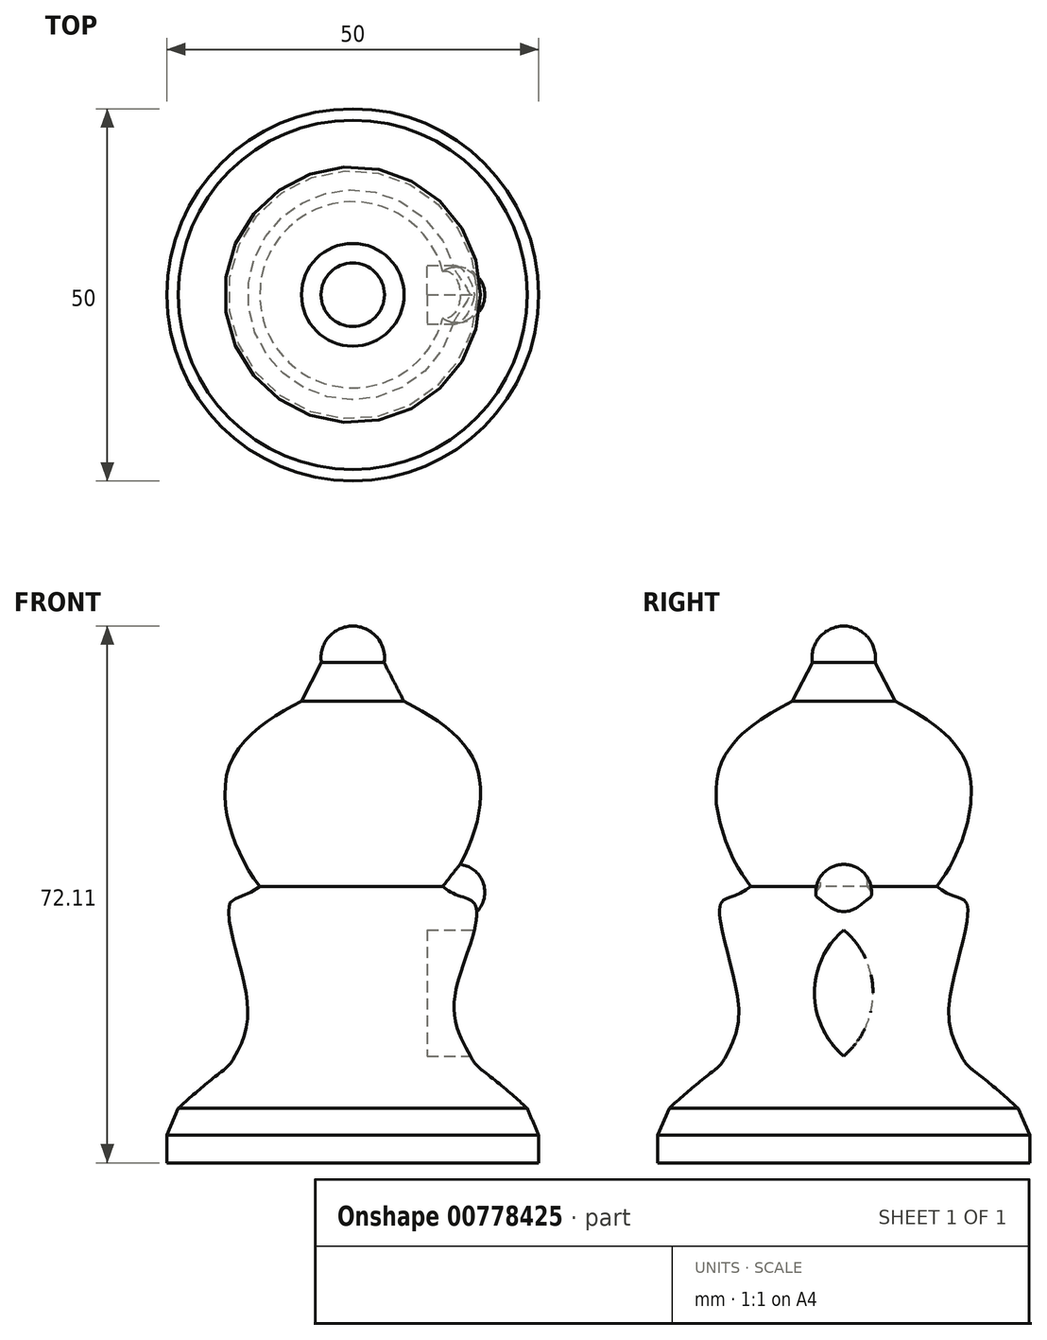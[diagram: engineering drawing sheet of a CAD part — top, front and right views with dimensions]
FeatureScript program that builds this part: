
annotation { "Feature Type Name" : "Feature", "Feature Type Description" : "" }
export const myFeature = defineFeature(function(context is Context, id is Id, definition is map)
    precondition{}
    {
        {
            var Q0;
            Q0=qCreatedBy(makeId("Front.planeOp"),FACE);
            var sketch = newSketch(context, id + "F0", { "sketchPlane" : qUnion([Q0])});
            skLineSegment(sketch, "E0.bottom", {"start": v(0, 0) * mm, "end": v(25, 0) * mm});
            skLineSegment(sketch, "E0.right", {"start": v(25, 0) * mm, "end": v(25, 5.75) * mm});
            skFitSpline(sketch, "E1", {"points": [v(12.5, 37.1) * mm, v(16.59, 34.67) * mm, v(14.3, 22.47) * mm, v(16.59, 13) * mm], "startDerivative": vector(26.77, -20.1) * mm, "endDerivative": vector(18.4, -30.72) * mm});
            skPoint(sketch, "E2.1.internal.snap0", {"position": v(25, 53.36) * mm});
            skFitSpline(sketch, "E2", {"points": [v(12.5, 37.1) * mm, v(16.59, 53.36) * mm, v(0, 65.21) * mm], "startDerivative": vector(22.32, 29.12) * mm, "endDerivative": vector(-44.63, 20.16) * mm});
            skFitSpline(sketch, "E3", {"points": [v(16.59, 13) * mm, v(22.47, 8.23) * mm, v(25, 5.75) * mm], "startDerivative": vector(8.7, -5.97) * mm, "endDerivative": vector(5.16, -5.51) * mm});
            skPoint(sketch, "E4.third.point", {"position": v(0, 67.84) * mm});
            skLineSegment(sketch, "E5", {"start": v(0, 65.21) * mm, "end": v(0, 0) * mm});
            skArc(sketch, "E6", {"start": v(2.23, 64.2) * mm, "mid": v(4.1, 69) * mm, "end": v(0, 72.1) * mm});
            skLineSegment(sketch, "E7", {"start": v(0, 65.21) * mm, "end": v(0, 72.1) * mm});
            skLineSegment(sketch, "E8", {"start": v(16.59, 13) * mm, "end": v(0, 13) * mm});
            skLineSegment(sketch, "E9", {"start": v(12.5, 37.1) * mm, "end": v(0, 37.1) * mm});
            skPoint(sketch, "E10.2.internal.snap0", {"position": v(6.25, 37.1) * mm});
            skSolve(sketch);
        }
        {
            var Q0;
            Q0 = qSketchRegion(id + "F0", true);
            var Q1;
            Q1=sQuery(id+"F0.wireOp",EDGE,"E5");
            revolve(context, id + "F1", {"surfaceOperationType" : NewSurfaceOperationType.NEW, "entities" : qUnion([Q0]), "axis" : qUnion([Q1]), "revolveType" : RevolveType.FULL});
        }
        {
            var Q0;
            Q0=qCreatedBy(makeId("Right.planeOp"),FACE);
            cPlane(context, id + "F2", {"entities" : qUnion([Q0]), "cplaneType" : CPlaneType.OFFSET, "offset" : 14 * mm, "width" : 150 * mm, "height" : 150 * mm});
        }
        {
            var Q0;
            Q0=qCreatedBy(id+"F2.planeOp",FACE);
            var sketch = newSketch(context, id + "F3", { "sketchPlane" : qUnion([Q0])});
            skArc(sketch, "E11", {"start": v(3.75, 36.36) * mm, "mid": v(0, 40.11) * mm, "end": v(-3.75, 36.36) * mm});
            skLineSegment(sketch, "E12", {"start": v(-3.75, 36.36) * mm, "end": v(3.75, 36.36) * mm});
            skSolve(sketch);
        }
        {
            var Q0;
            Q0 = qSketchRegion(id + "F3", true);
            var Q1;
            Q1=sQuery(id+"F3.wireOp",EDGE,"E12");
            revolve(context, id + "F4", {"operationType" : NewBodyOperationType.ADD, "surfaceOperationType" : NewSurfaceOperationType.NEW, "entities" : qUnion([Q0]), "axis" : qUnion([Q1]), "revolveType" : RevolveType.FULL});
        }
        {
            var Q0;
            Q0=qCreatedBy(makeId("Right.planeOp"),FACE);
            cPlane(context, id + "F5", {"entities" : qUnion([Q0]), "cplaneType" : CPlaneType.OFFSET, "offset" : 20 * mm, "width" : 150 * mm, "height" : 150 * mm});
        }
        {
            var Q0;
            Q0=qCreatedBy(id+"F5.planeOp",FACE);
            var sketch = newSketch(context, id + "F6", { "sketchPlane" : qUnion([Q0])});
            skArc(sketch, "E13", {"start": v(0, 14.35) * mm, "mid": v(3.93, 22.83) * mm, "end": v(0, 31.3) * mm});
            skArc(sketch, "E14.MirrorCS", {"start": v(0, 14.35) * mm, "mid": v(-3.93, 22.83) * mm, "end": v(0, 31.3) * mm});
            skSolve(sketch);
        }
        {
            var Q0;
            Q0 = qSketchRegion(id + "F6", true);
            extrude(context, id + "F7", {"entities" : qUnion([Q0]), "operationType" : NewBodyOperationType.REMOVE, "oppositeDirection" : true, "depth" : 10 * mm, "offsetDistance" : 25 * mm});
        }
        {
            var Q0;
            Q0=makeQuery(id+"F1.opRevolve","SWEPT_EDGE",EDGE,{"disambiguationData":[OSD([sQuery(id+"F0.wireOp",EDGE,"E1"),sQuery(id+"F0.wireOp",EDGE,"E3"),sQuery(id+"F0.wireOp",EDGE,"E8")])]});
            fillet(context, id + "F8", {"entities" : qUnion([Q0]), "radius" : 5 * mm, "tangentPropagation" : true, "allowEdgeOverflow" : false});
        }
        {
            var Q0;
            Q0=makeQuery(id+"F1.opRevolve","SWEPT_EDGE",EDGE,{"disambiguationData":[OSD([sQuery(id+"F0.wireOp",EDGE,"E0.right"),sQuery(id+"F0.wireOp",EDGE,"E3")])]});
            chamfer(context, id + "F9", {"entities" : qUnion([Q0]), "width" : 5 * mm, "tangentPropagation" : true});
        }
        {
            var Q0;
            Q0=makeQuery(id+"F1.opRevolve","SWEPT_EDGE",EDGE,{"disambiguationData":[OSD([sQuery(id+"F0.wireOp",EDGE,"E2"),sQuery(id+"F0.wireOp",EDGE,"E6")])]});
            chamfer(context, id + "F10", {"entities" : qUnion([Q0]), "width" : 5 * mm, "tangentPropagation" : true});
        }
    });
